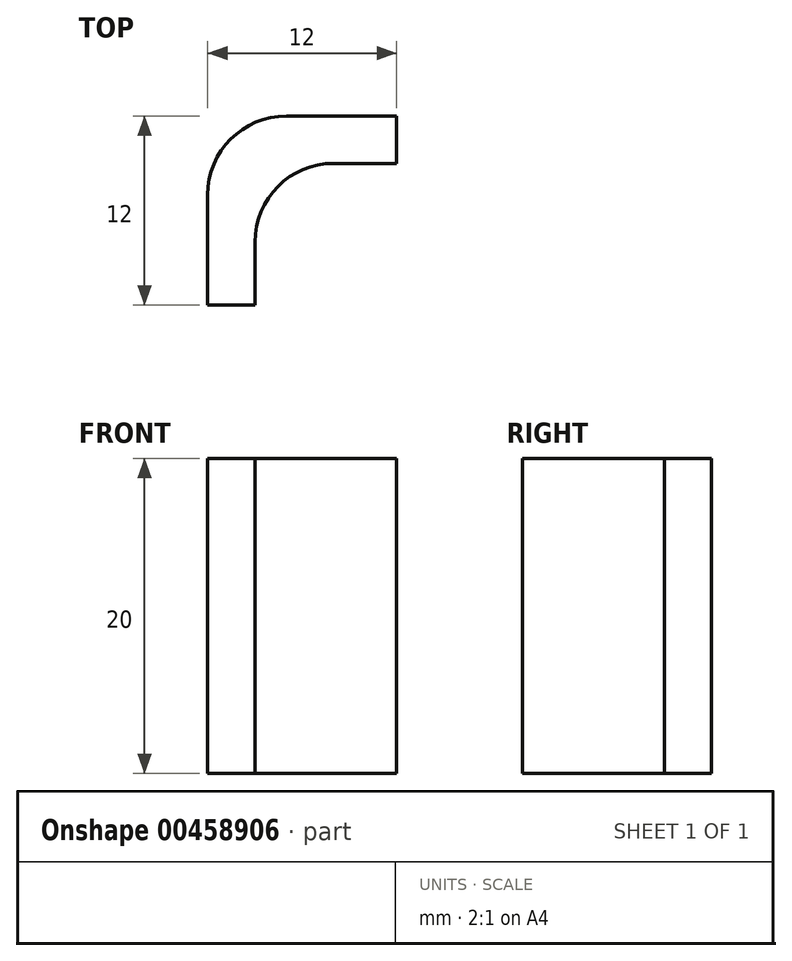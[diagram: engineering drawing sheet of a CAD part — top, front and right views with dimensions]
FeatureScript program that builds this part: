
annotation { "Feature Type Name" : "Feature", "Feature Type Description" : "" }
export const myFeature = defineFeature(function(context is Context, id is Id, definition is map)
    precondition{}
    {
        {
            var Q0;
            Q0=qCreatedBy(makeId("Top.planeOp"),FACE);
            var sketch = newSketch(context, id + "F0", { "sketchPlane" : qUnion([Q0])});
            skLineSegment(sketch, "E0", {"start": v(1.62, -9) * mm, "end": v(1.62, -5) * mm});
            skLineSegment(sketch, "E1", {"start": v(6.62, 0) * mm, "end": v(10.62, 0) * mm});
            skLineSegment(sketch, "E2", {"start": v(10.62, 0) * mm, "end": v(10.62, 3) * mm});
            skLineSegment(sketch, "E3", {"start": v(10.62, 3) * mm, "end": v(3.62, 3) * mm});
            skLineSegment(sketch, "E4", {"start": v(-1.38, -2) * mm, "end": v(-1.38, -9) * mm});
            skLineSegment(sketch, "E5", {"start": v(-1.38, -9) * mm, "end": v(1.62, -9) * mm});
            skPoint(sketch, "E6.visualSharp", {"position": v(-1.38, 3) * mm});
            skArc(sketch, "E6.filletArc", {"start": v(3.62, 3) * mm, "mid": v(0.09, 1.54) * mm, "end": v(-1.38, -2) * mm});
            skPoint(sketch, "E7.visualSharp", {"position": v(1.62, 0) * mm});
            skArc(sketch, "E7.filletArc", {"start": v(6.62, 0) * mm, "mid": v(3.09, -1.46) * mm, "end": v(1.62, -5) * mm});
            skSolve(sketch);
        }
        {
            var Q0;
            Q0 = qSketchRegion(id + "F0", true);
            extrude(context, id + "F1", {"entities" : qUnion([Q0]), "depth" : 20 * mm});
        }
    });
